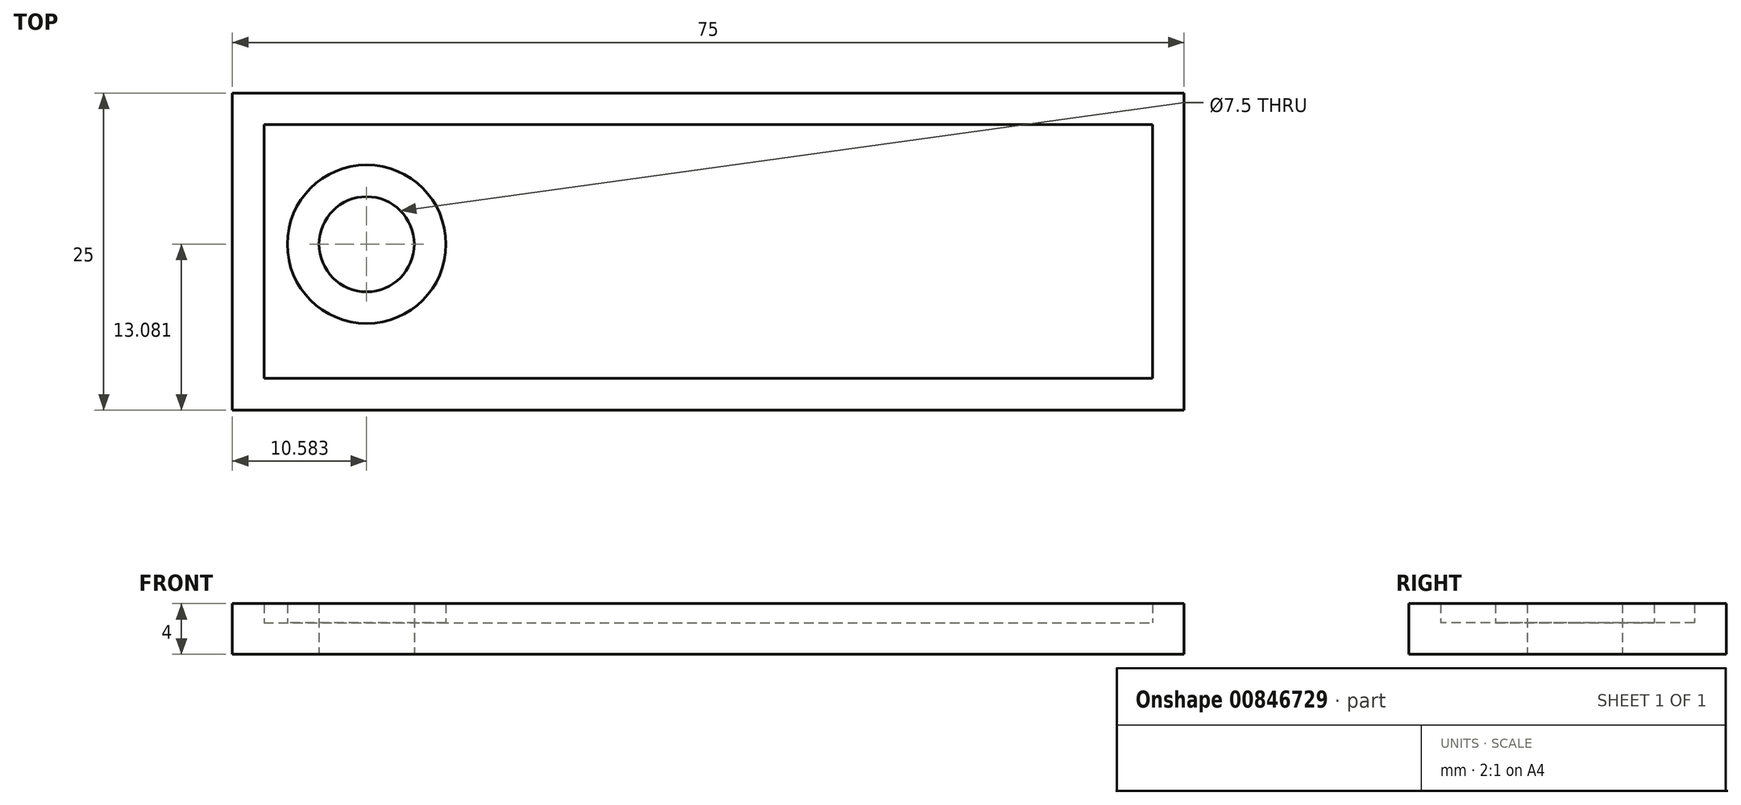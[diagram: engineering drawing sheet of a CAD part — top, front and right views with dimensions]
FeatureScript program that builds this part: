
annotation { "Feature Type Name" : "Feature", "Feature Type Description" : "" }
export const myFeature = defineFeature(function(context is Context, id is Id, definition is map)
    precondition{}
    {
        {
            var Q0;
            Q0=qCreatedBy(makeId("Top.planeOp"),FACE);
            var sketch = newSketch(context, id + "F0", { "sketchPlane" : qUnion([Q0])});
            skLineSegment(sketch, "E0.bottom", {"start": v(-68.06, 25) * mm, "end": v(6.94, 25) * mm});
            skLineSegment(sketch, "E0.top", {"start": v(-68.06, 0) * mm, "end": v(6.94, 0) * mm});
            skLineSegment(sketch, "E0.left", {"start": v(-68.06, 25) * mm, "end": v(-68.06, 0) * mm});
            skLineSegment(sketch, "E0.right", {"start": v(6.94, 25) * mm, "end": v(6.94, 0) * mm});
            skCircle(sketch, "E1", {"center": v(-57.48, 13.08) * mm, "radius": 3.75 * mm});
            skSolve(sketch);
        }
        {
            var Q0;
            Q0 = qSketchRegion(id + "F0", true);
            extrude(context, id + "F1", {"entities" : qUnion([Q0]), "depth" : 4 * mm, "offsetDistance" : 25 * mm});
        }
        {
            var Q0;
            Q0=makeQuery(id+"F1.opExtrude","CAP_FACE",FACE,{"disambiguationData":[OSD([sQuery(id+"F0.wireOp",EDGE,"E0.bottom"),sQuery(id+"F0.wireOp",EDGE,"E0.top"),sQuery(id+"F0.wireOp",EDGE,"E0.left"),sQuery(id+"F0.wireOp",EDGE,"E0.right"),sQuery(id+"F0.wireOp",EDGE,"ac21be8f-22cf-4286-9c54-5b9423a25561.sketch_text.stroke-0"),sQuery(id+"F0.wireOp",EDGE,"ac21be8f-22cf-4286-9c54-5b9423a25561.sketch_text.stroke-1"),sQuery(id+"F0.wireOp",EDGE,"ac21be8f-22cf-4286-9c54-5b9423a25561.sketch_text.stroke-2"),sQuery(id+"F0.wireOp",EDGE,"ac21be8f-22cf-4286-9c54-5b9423a25561.sketch_text.stroke-3"),sQuery(id+"F0.wireOp",EDGE,"ac21be8f-22cf-4286-9c54-5b9423a25561.sketch_text.stroke-4"),sQuery(id+"F0.wireOp",EDGE,"ac21be8f-22cf-4286-9c54-5b9423a25561.sketch_text.stroke-5"),sQuery(id+"F0.wireOp",EDGE,"ac21be8f-22cf-4286-9c54-5b9423a25561.sketch_text.stroke-6"),sQuery(id+"F0.wireOp",EDGE,"ac21be8f-22cf-4286-9c54-5b9423a25561.sketch_text.stroke-7"),sQuery(id+"F0.wireOp",EDGE,"ac21be8f-22cf-4286-9c54-5b9423a25561.sketch_text.stroke-15"),sQuery(id+"F0.wireOp",EDGE,"ac21be8f-22cf-4286-9c54-5b9423a25561.sketch_text.stroke-16"),sQuery(id+"F0.wireOp",EDGE,"ac21be8f-22cf-4286-9c54-5b9423a25561.sketch_text.stroke-17"),sQuery(id+"F0.wireOp",EDGE,"ac21be8f-22cf-4286-9c54-5b9423a25561.sketch_text.stroke-18"),sQuery(id+"F0.wireOp",EDGE,"ac21be8f-22cf-4286-9c54-5b9423a25561.sketch_text.stroke-19"),sQuery(id+"F0.wireOp",EDGE,"ac21be8f-22cf-4286-9c54-5b9423a25561.sketch_text.stroke-20"),sQuery(id+"F0.wireOp",EDGE,"ac21be8f-22cf-4286-9c54-5b9423a25561.sketch_text.stroke-21"),sQuery(id+"F0.wireOp",EDGE,"ac21be8f-22cf-4286-9c54-5b9423a25561.sketch_text.stroke-22"),sQuery(id+"F0.wireOp",EDGE,"ac21be8f-22cf-4286-9c54-5b9423a25561.sketch_text.stroke-23"),sQuery(id+"F0.wireOp",EDGE,"ac21be8f-22cf-4286-9c54-5b9423a25561.sketch_text.stroke-24"),sQuery(id+"F0.wireOp",EDGE,"ac21be8f-22cf-4286-9c54-5b9423a25561.sketch_text.stroke-25"),sQuery(id+"F0.wireOp",EDGE,"ac21be8f-22cf-4286-9c54-5b9423a25561.sketch_text.stroke-26"),sQuery(id+"F0.wireOp",EDGE,"ac21be8f-22cf-4286-9c54-5b9423a25561.sketch_text.stroke-27"),sQuery(id+"F0.wireOp",EDGE,"ac21be8f-22cf-4286-9c54-5b9423a25561.sketch_text.stroke-28"),sQuery(id+"F0.wireOp",EDGE,"ac21be8f-22cf-4286-9c54-5b9423a25561.sketch_text.stroke-29"),sQuery(id+"F0.wireOp",EDGE,"ac21be8f-22cf-4286-9c54-5b9423a25561.sketch_text.stroke-30"),sQuery(id+"F0.wireOp",EDGE,"ac21be8f-22cf-4286-9c54-5b9423a25561.sketch_text.stroke-31"),sQuery(id+"F0.wireOp",EDGE,"ac21be8f-22cf-4286-9c54-5b9423a25561.sketch_text.stroke-32"),sQuery(id+"F0.wireOp",EDGE,"ac21be8f-22cf-4286-9c54-5b9423a25561.sketch_text.stroke-33"),sQuery(id+"F0.wireOp",EDGE,"ac21be8f-22cf-4286-9c54-5b9423a25561.sketch_text.stroke-42"),sQuery(id+"F0.wireOp",EDGE,"ac21be8f-22cf-4286-9c54-5b9423a25561.sketch_text.stroke-43"),sQuery(id+"F0.wireOp",EDGE,"ac21be8f-22cf-4286-9c54-5b9423a25561.sketch_text.stroke-44"),sQuery(id+"F0.wireOp",EDGE,"ac21be8f-22cf-4286-9c54-5b9423a25561.sketch_text.stroke-45"),sQuery(id+"F0.wireOp",EDGE,"ac21be8f-22cf-4286-9c54-5b9423a25561.sketch_text.stroke-46"),sQuery(id+"F0.wireOp",EDGE,"ac21be8f-22cf-4286-9c54-5b9423a25561.sketch_text.stroke-47"),sQuery(id+"F0.wireOp",EDGE,"ac21be8f-22cf-4286-9c54-5b9423a25561.sketch_text.stroke-48"),sQuery(id+"F0.wireOp",EDGE,"ac21be8f-22cf-4286-9c54-5b9423a25561.sketch_text.stroke-49"),sQuery(id+"F0.wireOp",EDGE,"ac21be8f-22cf-4286-9c54-5b9423a25561.sketch_text.stroke-50"),sQuery(id+"F0.wireOp",EDGE,"ac21be8f-22cf-4286-9c54-5b9423a25561.sketch_text.stroke-51"),sQuery(id+"F0.wireOp",EDGE,"ac21be8f-22cf-4286-9c54-5b9423a25561.sketch_text.stroke-52"),sQuery(id+"F0.wireOp",EDGE,"ac21be8f-22cf-4286-9c54-5b9423a25561.sketch_text.stroke-53"),sQuery(id+"F0.wireOp",EDGE,"ac21be8f-22cf-4286-9c54-5b9423a25561.sketch_text.stroke-54"),sQuery(id+"F0.wireOp",EDGE,"ac21be8f-22cf-4286-9c54-5b9423a25561.sketch_text.stroke-55"),sQuery(id+"F0.wireOp",EDGE,"ac21be8f-22cf-4286-9c54-5b9423a25561.sketch_text.stroke-56"),sQuery(id+"F0.wireOp",EDGE,"ac21be8f-22cf-4286-9c54-5b9423a25561.sketch_text.stroke-57"),sQuery(id+"F0.wireOp",EDGE,"ac21be8f-22cf-4286-9c54-5b9423a25561.sketch_text.stroke-58"),sQuery(id+"F0.wireOp",EDGE,"ac21be8f-22cf-4286-9c54-5b9423a25561.sketch_text.stroke-59"),sQuery(id+"F0.wireOp",EDGE,"ac21be8f-22cf-4286-9c54-5b9423a25561.sketch_text.stroke-60"),sQuery(id+"F0.wireOp",EDGE,"ac21be8f-22cf-4286-9c54-5b9423a25561.sketch_text.stroke-61"),sQuery(id+"F0.wireOp",EDGE,"ac21be8f-22cf-4286-9c54-5b9423a25561.sketch_text.stroke-62"),sQuery(id+"F0.wireOp",EDGE,"c6e3a6f3-eab9-48bb-a127-c734186dc3f5.sketch_text.stroke-0"),sQuery(id+"F0.wireOp",EDGE,"c6e3a6f3-eab9-48bb-a127-c734186dc3f5.sketch_text.stroke-1"),sQuery(id+"F0.wireOp",EDGE,"c6e3a6f3-eab9-48bb-a127-c734186dc3f5.sketch_text.stroke-2"),sQuery(id+"F0.wireOp",EDGE,"c6e3a6f3-eab9-48bb-a127-c734186dc3f5.sketch_text.stroke-3"),sQuery(id+"F0.wireOp",EDGE,"c6e3a6f3-eab9-48bb-a127-c734186dc3f5.sketch_text.stroke-4"),sQuery(id+"F0.wireOp",EDGE,"c6e3a6f3-eab9-48bb-a127-c734186dc3f5.sketch_text.stroke-5"),sQuery(id+"F0.wireOp",EDGE,"c6e3a6f3-eab9-48bb-a127-c734186dc3f5.sketch_text.stroke-6"),sQuery(id+"F0.wireOp",EDGE,"c6e3a6f3-eab9-48bb-a127-c734186dc3f5.sketch_text.stroke-7"),sQuery(id+"F0.wireOp",EDGE,"c6e3a6f3-eab9-48bb-a127-c734186dc3f5.sketch_text.stroke-8"),sQuery(id+"F0.wireOp",EDGE,"c6e3a6f3-eab9-48bb-a127-c734186dc3f5.sketch_text.stroke-14"),sQuery(id+"F0.wireOp",EDGE,"c6e3a6f3-eab9-48bb-a127-c734186dc3f5.sketch_text.stroke-15"),sQuery(id+"F0.wireOp",EDGE,"c6e3a6f3-eab9-48bb-a127-c734186dc3f5.sketch_text.stroke-17"),sQuery(id+"F0.wireOp",EDGE,"c6e3a6f3-eab9-48bb-a127-c734186dc3f5.sketch_text.stroke-18"),sQuery(id+"F0.wireOp",EDGE,"c6e3a6f3-eab9-48bb-a127-c734186dc3f5.sketch_text.stroke-19"),sQuery(id+"F0.wireOp",EDGE,"c6e3a6f3-eab9-48bb-a127-c734186dc3f5.sketch_text.stroke-20"),sQuery(id+"F0.wireOp",EDGE,"c6e3a6f3-eab9-48bb-a127-c734186dc3f5.sketch_text.stroke-21"),sQuery(id+"F0.wireOp",EDGE,"c6e3a6f3-eab9-48bb-a127-c734186dc3f5.sketch_text.stroke-22"),sQuery(id+"F0.wireOp",EDGE,"c6e3a6f3-eab9-48bb-a127-c734186dc3f5.sketch_text.stroke-23"),sQuery(id+"F0.wireOp",EDGE,"c6e3a6f3-eab9-48bb-a127-c734186dc3f5.sketch_text.stroke-24"),sQuery(id+"F0.wireOp",EDGE,"c6e3a6f3-eab9-48bb-a127-c734186dc3f5.sketch_text.stroke-25"),sQuery(id+"F0.wireOp",EDGE,"c6e3a6f3-eab9-48bb-a127-c734186dc3f5.sketch_text.stroke-26"),sQuery(id+"F0.wireOp",EDGE,"c6e3a6f3-eab9-48bb-a127-c734186dc3f5.sketch_text.stroke-27"),sQuery(id+"F0.wireOp",EDGE,"c6e3a6f3-eab9-48bb-a127-c734186dc3f5.sketch_text.stroke-28"),sQuery(id+"F0.wireOp",EDGE,"c6e3a6f3-eab9-48bb-a127-c734186dc3f5.sketch_text.stroke-34"),sQuery(id+"F0.wireOp",EDGE,"c6e3a6f3-eab9-48bb-a127-c734186dc3f5.sketch_text.stroke-35"),sQuery(id+"F0.wireOp",EDGE,"c6e3a6f3-eab9-48bb-a127-c734186dc3f5.sketch_text.stroke-37"),sQuery(id+"F0.wireOp",EDGE,"c6e3a6f3-eab9-48bb-a127-c734186dc3f5.sketch_text.stroke-38"),sQuery(id+"F0.wireOp",EDGE,"c6e3a6f3-eab9-48bb-a127-c734186dc3f5.sketch_text.stroke-39"),sQuery(id+"F0.wireOp",EDGE,"c6e3a6f3-eab9-48bb-a127-c734186dc3f5.sketch_text.stroke-40"),sQuery(id+"F0.wireOp",EDGE,"c6e3a6f3-eab9-48bb-a127-c734186dc3f5.sketch_text.stroke-41"),sQuery(id+"F0.wireOp",EDGE,"c6e3a6f3-eab9-48bb-a127-c734186dc3f5.sketch_text.stroke-42"),sQuery(id+"F0.wireOp",EDGE,"c6e3a6f3-eab9-48bb-a127-c734186dc3f5.sketch_text.stroke-43"),sQuery(id+"F0.wireOp",EDGE,"c6e3a6f3-eab9-48bb-a127-c734186dc3f5.sketch_text.stroke-44"),sQuery(id+"F0.wireOp",EDGE,"c6e3a6f3-eab9-48bb-a127-c734186dc3f5.sketch_text.stroke-45"),sQuery(id+"F0.wireOp",EDGE,"c6e3a6f3-eab9-48bb-a127-c734186dc3f5.sketch_text.stroke-46"),sQuery(id+"F0.wireOp",EDGE,"c6e3a6f3-eab9-48bb-a127-c734186dc3f5.sketch_text.stroke-47"),sQuery(id+"F0.wireOp",EDGE,"c6e3a6f3-eab9-48bb-a127-c734186dc3f5.sketch_text.stroke-48"),sQuery(id+"F0.wireOp",EDGE,"c6e3a6f3-eab9-48bb-a127-c734186dc3f5.sketch_text.stroke-49"),sQuery(id+"F0.wireOp",EDGE,"c6e3a6f3-eab9-48bb-a127-c734186dc3f5.sketch_text.stroke-50"),sQuery(id+"F0.wireOp",EDGE,"c6e3a6f3-eab9-48bb-a127-c734186dc3f5.sketch_text.stroke-51"),sQuery(id+"F0.wireOp",EDGE,"c6e3a6f3-eab9-48bb-a127-c734186dc3f5.sketch_text.stroke-52"),sQuery(id+"F0.wireOp",EDGE,"c6e3a6f3-eab9-48bb-a127-c734186dc3f5.sketch_text.stroke-53"),sQuery(id+"F0.wireOp",EDGE,"c6e3a6f3-eab9-48bb-a127-c734186dc3f5.sketch_text.stroke-54"),sQuery(id+"F0.wireOp",EDGE,"c6e3a6f3-eab9-48bb-a127-c734186dc3f5.sketch_text.stroke-55")])],"isStart":false});
            shell(context, id + "F2", {"entities" : qUnion([Q0]), "thickness" : 2.5 * mm});
        }
    });
